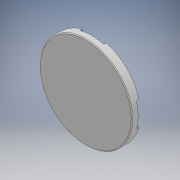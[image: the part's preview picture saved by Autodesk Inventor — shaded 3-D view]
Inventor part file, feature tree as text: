
AUTODESK INVENTOR PART (.ipt)
format: ipt  version: 2018 (Build 220112000, 112)  size: 337,920 bytes
history: native  units: mm
features: extrude x6, sketch x6, fillet x4, pattern_circular x2
ambient origin geometry x8: Origin, YZ Plane, XZ Plane, XY Plane, X Axis, Y Axis, Z Axis, Center Point
bodies: Solid1 (feature_tree)
feature tree (18):
  extrude  "Extrusion1"  Depth=56.0mm
  extrude  "Extrusion2"  Depth=58.0mm
  extrude  "Extrusion3"  Depth=28.0mm
  fillet  "Fillet1"  Radius=22.514747mm
  pattern_circular  "Circular Pattern1"  [2 undecoded]
  extrude  "Extrusion4"  Depth=1.4mm TaperAngle=0.0deg
  fillet  "Fillet2"  Radius=0.5mm
  extrude  "Extrusion5"  Depth=20.0mm TaperAngle=360.0deg
  extrude  "Extrusion6"  Depth=3.0mm
  fillet  "Fillet3"  Radius=7.5mm
  fillet  "Fillet4"  Radius=3.0mm
  pattern_circular  "Circular Pattern2"  [2 undecoded]
  sketch  "Sketch1"  dims[d2=0.4mm d3=0.0mm d4=56.0mm]
  sketch  "Sketch2"  dims[d5=5.0mm d6=0.0mm d7=58.0mm]
  sketch  "Sketch3"  dims[d8=58.0mm d9=28.0mm d10=22.514747mm]
  sketch  "Sketch4"  dims[d11=0.698132mm]
  sketch  "Sketch5"  dims[d12=27.0mm]
  sketch  "Sketch6"  dims[d13=22.514747mm d14=0.698132mm d15=1.4mm d16=0.0mm d17=0.5mm d18=20.0mm d19=360.0deg d21=3.0mm d22=7.5mm d23=3.0mm d24=7.5mm d25=7.5mm d26=3.0mm d27=7.5mm d28=3.0mm d29=1.5mm d30=0.0mm d31=0.5mm d32=24.5mm d33=17.453293mm d34=3.490659mm d35=28.5mm d36=17.453293mm d37=3.490659mm d38=4.0mm d39=0.0mm d40=3.0mm d41=0.0mm d42=1.0mm d43=0.5mm d44=30.0mm d45=360.0deg]
note: 4 required parameter values undecoded (feature->parameter linkage not recoverable at this tier; creation-order binding heuristic only, values carry confidence <= 0.55)
